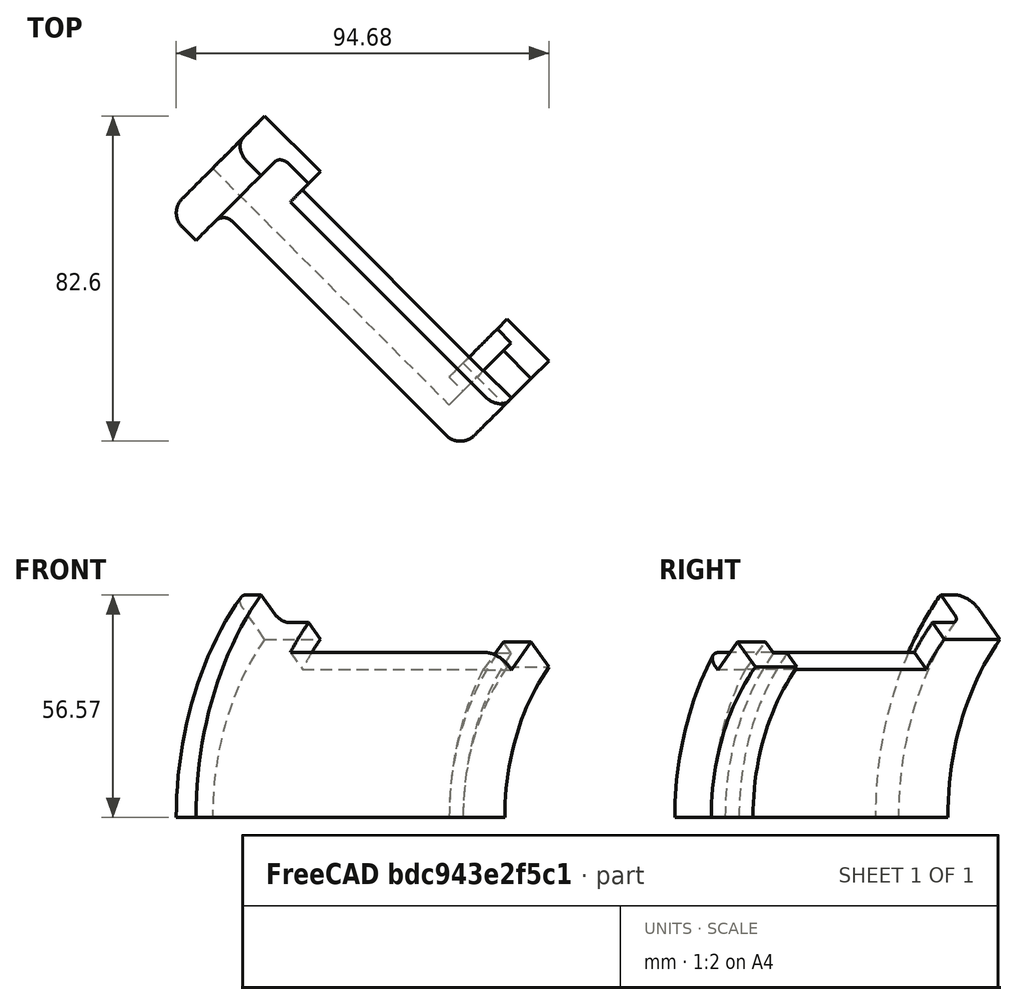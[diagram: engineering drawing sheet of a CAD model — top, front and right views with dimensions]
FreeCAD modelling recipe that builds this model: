
FCSTD DOCUMENT  (FreeCAD 0.15R4671 (Git))
Label: sphere_support_cyls4_w4
License: All rights reserved
LicenseURL: http://en.wikipedia.org/wiki/All_rights_reserved
objects: Part::Cut×11, Part::Box×8, Part::Cylinder×6, Part::Fillet×3, Part::MultiFuse×2
note: 30 computed .brp shape members not serialized (recipe doc carries the construction recipe); baked Part::Feature solids carry a one-line shape summary decoded from their .brp

FEATURE [Part::Cylinder] Cylinder  label="Base_Cylinder"
  Angle = 360
  Height = 10
  Radius = 80
FEATURE [Part::Cylinder] Cylinder001  label="Body_Cylinder"
  Angle = 360
  Height = 90
  Placement = pos=(0,0,5) rot=(0,0,1;0rad)
  Radius = 70
FEATURE [Part::MultiFuse] Fusion  label="Core_Fusion"
  Shapes = -> [Cylinder,Cylinder001]
FEATURE [Part::Cylinder] Cylinder002  label="Inner_Hole"
  Angle = 360
  Height = 85
  Radius = 64
FEATURE [Part::Cut] Cut
  Base = -> Fusion
  Tool = -> Cylinder002
FEATURE [Part::Cylinder] Cylinder003  label="Inner_Lip"
  Angle = 360
  Height = 10
  Placement = pos=(0,0,80) rot=(0,0,1;0rad)
  Radius = 59
FEATURE [Part::MultiFuse] Fusion001
  Shapes = -> [Cut,Cylinder003]
FEATURE [Part::Cylinder] Cylinder004  label="Through_Hole"
  Angle = 360
  Height = 100
  Radius = 54
FEATURE [Part::Cut] Cut001
  Base = -> Fusion001
  Tool = -> Cylinder004
FEATURE [Part::Fillet] Fillet
  Base = -> Cut001
  Edges = 1 edges r=3: [Edge12]
FEATURE [Part::Fillet] Fillet001
  Base = -> Fillet
  Edges = 1 edges r=5: [Edge11]
FEATURE [Part::Fillet] Fillet002
  Base = -> Fillet001
  Edges = 1 edges r=5: [Edge13]
FEATURE [Part::Cylinder] Cylinder005  label="Bearing_Holes"
  Angle = 360
  Height = 180
  Placement = pos=(0,90,65) rot=(1,0,0;1.5708rad)
  Radius = 10
FEATURE [Part::Cut] Cut002
  Base = -> Fillet002
  Tool = -> Cylinder005
FEATURE [Part::Box] Box  label="Bearing_Slot"
  Height = 35
  Length = 20
  Placement = pos=(-10,48,65) rot=(0,0,1;0rad)
  Width = 25
FEATURE [Part::Cut] Cut003
  Base = -> Cut002
  Tool = -> Box
FEATURE [Part::Box] Box001  label="Cube"
  Height = 35
  Length = 10
  Placement = pos=(0,48,65) rot=(0,1,0;0.261799rad)
  Width = 25
FEATURE [Part::Cut] Cut004
  Base = -> Cut003
  Tool = -> Box001
FEATURE [Part::Box] Box002  label="Cube001"
  Height = 35
  Length = 10
  Placement = pos=(-9.95,48,64) rot=(0,-1,0;0.261799rad)
  Width = 25
FEATURE [Part::Cut] Cut005
  Base = -> Cut004
  Tool = -> Box002
FEATURE [Part::Box] Box003  label="Tab_Cut_R"
  Height = 80
  Length = 20
  Placement = pos=(63,-10,20) rot=(0,0,1;0rad)
  Width = 20
FEATURE [Part::Cut] Cut006
  Base = -> Cut005
  Tool = -> Box003
FEATURE [Part::Box] Box004  label="Tab_Cut_L"
  Height = 80
  Length = 20
  Placement = pos=(-83,-10,20) rot=(0,0,1;0rad)
  Width = 20
FEATURE [Part::Cut] Cut007
  Base = -> Cut006
  Placement = pos=(0,0,0) rot=(0.707107,0.707107,0;1.5708rad)
  Tool = -> Box004
FEATURE [Part::Box] Box005  label="Cube002"
  Height = 100
  Length = 200
  Placement = pos=(-70,-120,-100) rot=(0,0,1;0rad)
  Width = 200
FEATURE [Part::Cut] Cut008
  Base = -> Cut007
  Placement = pos=(0,0,0) rot=(-0.707107,-0.707107,0;1.5708rad)
  Tool = -> Box005
FEATURE [Part::Box] Box006  label="Cube003"
  Height = 100
  Length = 100
  Placement = pos=(0,0,0) rot=(0,0,1;1.5708rad)
  Width = 100
FEATURE [Part::Cut] Cut009
  Base = -> Cut008
  Tool = -> Box006
FEATURE [Part::Box] Box007  label="Cube004"
  Height = 100
  Length = 100
  Width = 100
FEATURE [Part::Cut] Cut010
  Base = -> Cut009
  Placement = pos=(0,0,0) rot=(0.707107,0.707107,0;1.5708rad)
  Tool = -> Box007
